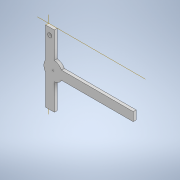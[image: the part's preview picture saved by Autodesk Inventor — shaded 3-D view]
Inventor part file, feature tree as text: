
AUTODESK INVENTOR PART (.ipt)
format: ipt  version: 2022 (Build 260153000, 153)  size: 114,688 bytes
history: native  units: mm
features: other x1, extrude x1, sketch x1
ambient origin geometry x8: Origin, YZ Plane, XZ Plane, XY Plane, X Axis, Y Axis, Z Axis, Center Point
bodies: Body1 (feature_tree)
feature tree (3):
  other  "Sólido1"
  extrude  "Extrusión1"  Depth=5.0mm TaperAngle=0.0deg
  sketch  "Boceto1"  dims[d0=2.0mm d1=5.0mm d2=0.0mm]
